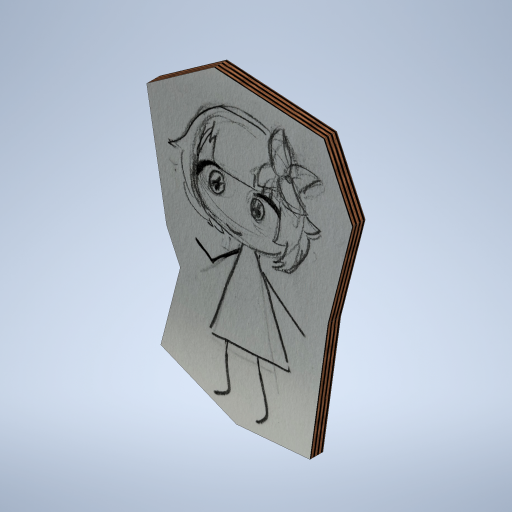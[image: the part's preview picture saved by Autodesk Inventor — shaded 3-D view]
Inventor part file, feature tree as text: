
AUTODESK INVENTOR PART (.ipt)
format: ipt  version: 2023 (Build 270158000, 158)  size: 1,271,808 bytes
history: native  units: in
note: dims shown in document units (in); Inventor stores cm internally (conversion verified against a paired STEP export)
features: extrude x1, sketch x1, other x1
ambient origin geometry x8: Origin, YZ Plane, XZ Plane, XY Plane, X Axis, Y Axis, Z Axis, Center Point
bodies: Solid1 (feature_tree)
feature tree (3):
  extrude  "Extrusion1"  Depth=1.0in
  sketch  "Sketch1"  dims[d5=1.0in d6=0.0in d7=15.8831in d10=22.842in]
  other  "Image1"
